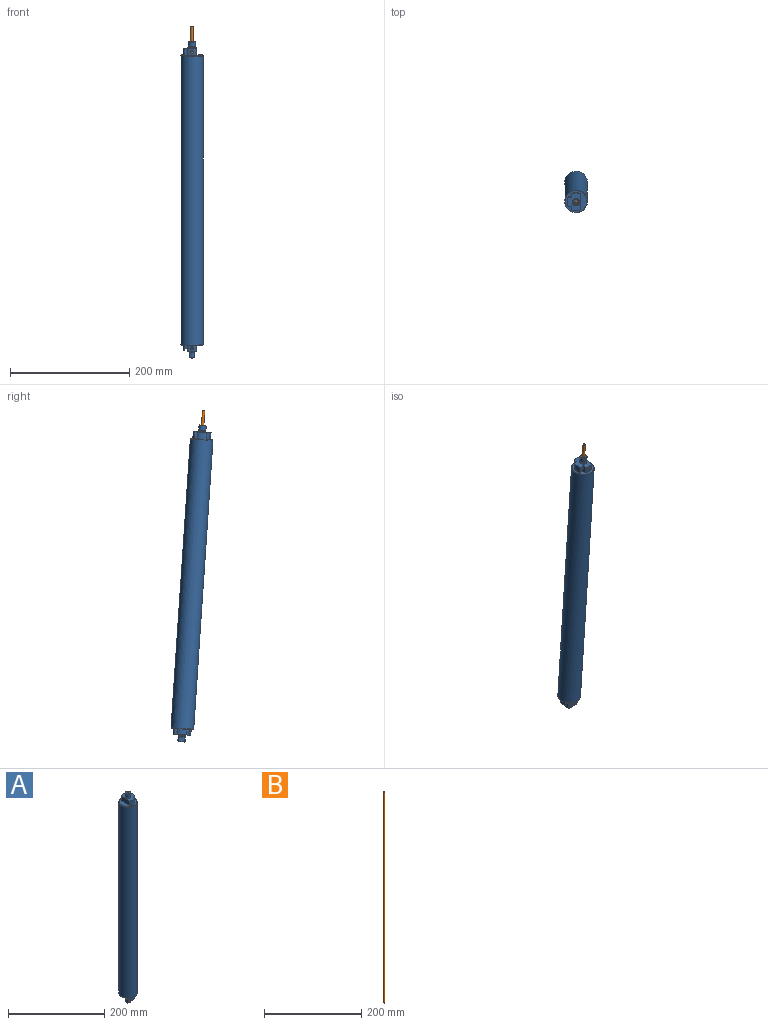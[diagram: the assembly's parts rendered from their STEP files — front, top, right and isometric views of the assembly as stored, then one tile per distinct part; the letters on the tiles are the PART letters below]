
ASSEMBLY  parts=2 mates=1
PART A: 71 faces, bbox 38.1x38.1x532 mm
  f0: plane 15x11.08mm, normal (0,0,-1), area 87.1mm2, adj f17,f26,f46,f50,f57,f58,f61,f62
  f1: plane 15x11.08mm, normal (0,0,-1), area 87.1mm2, adj f18,f19,f22,f50,f57,f59,f61,f63
  f2: plane 10x8mm, normal (0,0,-1), area 57.8mm2, adj f3,f4,f57,f61,f65
  f3: cone r=5mm half-angle=45deg, axis (0,0,1), area 12.7mm2, adj f2,f6,f57,f61
  f4: cone r=5mm half-angle=45deg, axis (0,0,1), area 12.7mm2, adj f2,f5,f57,f61
  f5: cylinder r=6mm len=8mm, axis (0,0,-1), area 67.9mm2, adj f4,f7,f57,f61
  f6: cylinder r=6mm len=8mm, axis (0,0,-1), area 67.9mm2, adj f3,f8,f57,f61
  f7: plane 8x2.68mm, normal (0,0,1), area 7.1mm2, adj f5,f9,f57,f61
  f8: plane 8x2.68mm, normal (0,0,1), area 7.1mm2, adj f6,f10,f57,f61
  f9: cylinder r=5.2mm len=8mm, axis (0,0,-1), area 13.7mm2, adj f7,f12,f57,f61
  f10: cylinder r=5.2mm len=8mm, axis (0,0,-1), area 13.7mm2, adj f8,f11,f57,f61
  f11: plane 8x2.68mm, normal (0,0,-1), area 7.1mm2, adj f10,f14,f57,f61
  f12: plane 8x2.68mm, normal (0,0,-1), area 7.1mm2, adj f9,f13,f57,f61
  f13: cylinder r=6mm len=8mm, axis (0,0,-1), area 8.8mm2, adj f12,f15,f57,f61
  f14: cylinder r=6mm len=8mm, axis (0,0,-1), area 8.8mm2, adj f11,f16,f57,f61
  f15: plane 8x2.08mm, normal (0,0,1), area 3.5mm2, adj f13,f17,f57,f61
  f16: plane 8x2.08mm, normal (0,0,1), area 3.5mm2, adj f14,f18,f57,f61
  f17: cylinder r=5.6mm len=8mm, axis (0,0,-1), area 6.7mm2, adj f0,f15,f57,f61
  f18: cylinder r=5.6mm len=8mm, axis (0,0,-1), area 6.7mm2, adj f1,f16,f57,f61
  f19: plane 9.5x5.49mm, normal (1,0,0), area 32.2mm2, adj f1,f22,f27,f52,f56,f59
  f20: cylinder r=15mm len=15mm, axis (0,0,-1), area 180.6mm2, adj f21,f33,f51,f53
  f21: plane 30x22.5mm, normal (0,0,1), area 434.7mm2, adj f20,f23,f34,f35,f48,f49,f51,f53
  f22: cylinder r=15mm len=15mm, axis (0,0,-1), area 149.2mm2, adj f1,f19,f27,f50
  f23: cylinder r=15mm len=15mm, axis (0,0,-1), area 180.6mm2, adj f21,f33,f48,f54
  f24: cylinder r=15mm len=15mm, axis (0,0,-1), area 149.2mm2, adj f25,f27,f47,f52
  f25: plane 15x2.5mm, normal (0,0,-1), area 27.7mm2, adj f24,f47,f52,f55
  f26: cylinder r=15mm len=15mm, axis (0,0,-1), area 129.5mm2, adj f0,f27,f46,f50,f66
  f27: plane 36.6x36.6mm, normal (0,0,-1), area 518.9mm2, adj f19,f22,f24,f26,f28,f46,f47,f50
  f28: cylinder r=18.3mm len=36.6mm, axis (0,0,-1), area 115mm2, adj f27,f29
  f29: plane 38.1x38.1mm, normal (0,0,-1), area 88mm2, adj f28,f30
  f30: cylinder r=19.05mm len=485mm, axis (0,0,-1), area 58051.9mm2, adj f29,f31
  f31: plane 38.1x38.1mm, normal (0,0,1), area 88mm2, adj f30,f32
  f32: cylinder r=18.3mm len=36.6mm, axis (0,0,-1), area 115mm2, adj f31,f33
  f33: plane 36.6x36.6mm, normal (0,0,1), area 518.9mm2, adj f20,f23,f32,f34,f48,f49,f51,f53
  f34: cylinder r=15mm len=15mm, axis (0,0,-1), area 161mm2, adj f21,f33,f49,f51,f69
  f35: cylinder r=5.6mm len=11.2mm, axis (0,0,-1), area 26.4mm2, adj f21,f36
  f36: plane 12x12mm, normal (0,0,-1), area 14.6mm2, adj f35,f37
  f37: cylinder r=6mm len=12mm, axis (0,0,-1), area 37.7mm2, adj f36,f38
  f38: plane 12x12mm, normal (0,0,1), area 28.1mm2, adj f37,f39
  f39: cylinder r=5.2mm len=10.4mm, axis (0,0,-1), area 49mm2, adj f38,f40
  f40: plane 12x12mm, normal (0,0,-1), area 28.1mm2, adj f39,f41
  f41: cylinder r=6mm len=12mm, axis (0,0,-1), area 292.2mm2, adj f40,f42
  f42: cone r=6mm half-angle=45deg, axis (0,0,-1), area 48.9mm2, adj f41,f43
  f43: plane 10x10mm, normal (0,0,1), area 66mm2, adj f42,f44
  f44: cylinder r=2mm len=510.5mm, axis (0,0,-1), area 6389.6mm2, adj f43,f45,f68,f69,f70
  f45: plane 4x4mm, normal (0,0,1), area 12.6mm2, adj f44
  f46: plane 9.5x5.49mm, normal (1,0,0), area 32.2mm2, adj f0,f26,f27,f47,f56,f58
  f47: plane 9.5x5.49mm, normal (0,1,0), area 32.2mm2, adj f24,f25,f27,f46,f55,f56
  f48: plane 11.5x5.49mm, normal (0,1,0), area 63.1mm2, adj f21,f23,f33,f49
  f49: plane 11.5x5.49mm, normal (1,0,0), area 63.1mm2, adj f21,f33,f34,f48
  f50: plane 25.98x9.5mm, normal (-1,0,0), area 146.8mm2, adj f0,f1,f22,f26,f27,f60,f62,f63
  f51: plane 25.98x11.5mm, normal (-1,0,0), area 298.8mm2, adj f20,f21,f33,f34
  f52: plane 9.5x5.49mm, normal (0,-1,0), area 32.2mm2, adj f19,f24,f25,f27,f55,f56
  f53: plane 11.5x5.49mm, normal (1,0,0), area 63.1mm2, adj f20,f21,f33,f54
  f54: plane 11.5x5.49mm, normal (0,-1,0), area 63.1mm2, adj f21,f23,f33,f53
  f55: plane 15x4mm, normal (-1,0,0), area 60mm2, adj f25,f47,f52,f56
  f56: plane 25x8.5mm, normal (0,0,-1), area 162.5mm2, adj f19,f46,f47,f52,f55,f57,f58,f59
  f57: plane 25x16mm, normal (1,0,0), area 189.1mm2, adj f0,f1,f2,f3,f4,f5,f6,f7
  f58: plane 4x3.5mm, normal (0,-1,0), area 14mm2, adj f0,f46,f56,f57
  f59: plane 4x3.5mm, normal (0,1,0), area 14mm2, adj f1,f19,f56,f57
  f60: plane 25x3.5mm, normal (0,0,-1), area 87.5mm2, adj f50,f61,f62,f63
  f61: plane 25x16mm, normal (-1,0,0), area 189.1mm2, adj f0,f1,f2,f3,f4,f5,f6,f7
  f62: plane 4x3.5mm, normal (0,-1,0), area 14mm2, adj f0,f50,f60,f61
  f63: plane 4x3.5mm, normal (0,1,0), area 14mm2, adj f1,f50,f60,f61
  f64: cylinder r=2mm len=8mm, axis (1,0,0), area 84.5mm2, adj f57,f61,f65
  f65: cylinder r=2mm len=10mm, axis (0,0,-1), area 109.7mm2, adj f2,f64
  f66: cylinder r=2.5mm len=15mm, axis (0,-1,0), area 234mm2, adj f26,f67
  f67: plane 5x5mm, normal (0,1,0), area 19.6mm2, adj f66
  f68: plane 3x0.5mm, normal (0,1,0), area 1mm2, adj f44,f69
  f69: cylinder r=2.5mm len=15mm, axis (0,-1,0), area 220mm2, adj f34,f44,f68,f70
  f70: plane 3x0.5mm, normal (0,1,0), area 1mm2, adj f44,f69
PART B: 4 faces, bbox 4x4x532 mm
  f0: plane 3x3mm, normal (0,0,1), area 7.1mm2, adj f3
  f1: cylinder r=2mm len=531.5mm, axis (0,0,1), area 6679mm2, adj f2,f3
  f2: plane 4x4mm, normal (0,0,-1), area 12.6mm2, adj f1
  f3: cone r=1.5mm half-angle=45deg, axis (0,0,-1), area 7.8mm2, adj f0,f1
PLACE A rot(axis=(0,0.03,-1),180deg) t=(-15.41,3.31,0.2)mm fixed
PLACE B rot(axis=(0.03,-0.03,1),96.1deg) t=(-15.41,2.69,9.6)mm
MATE cylindrical A.f3 <-> B.f1  axis (0,0.07,-1) through (-15.41,1.88,21.65)mm
